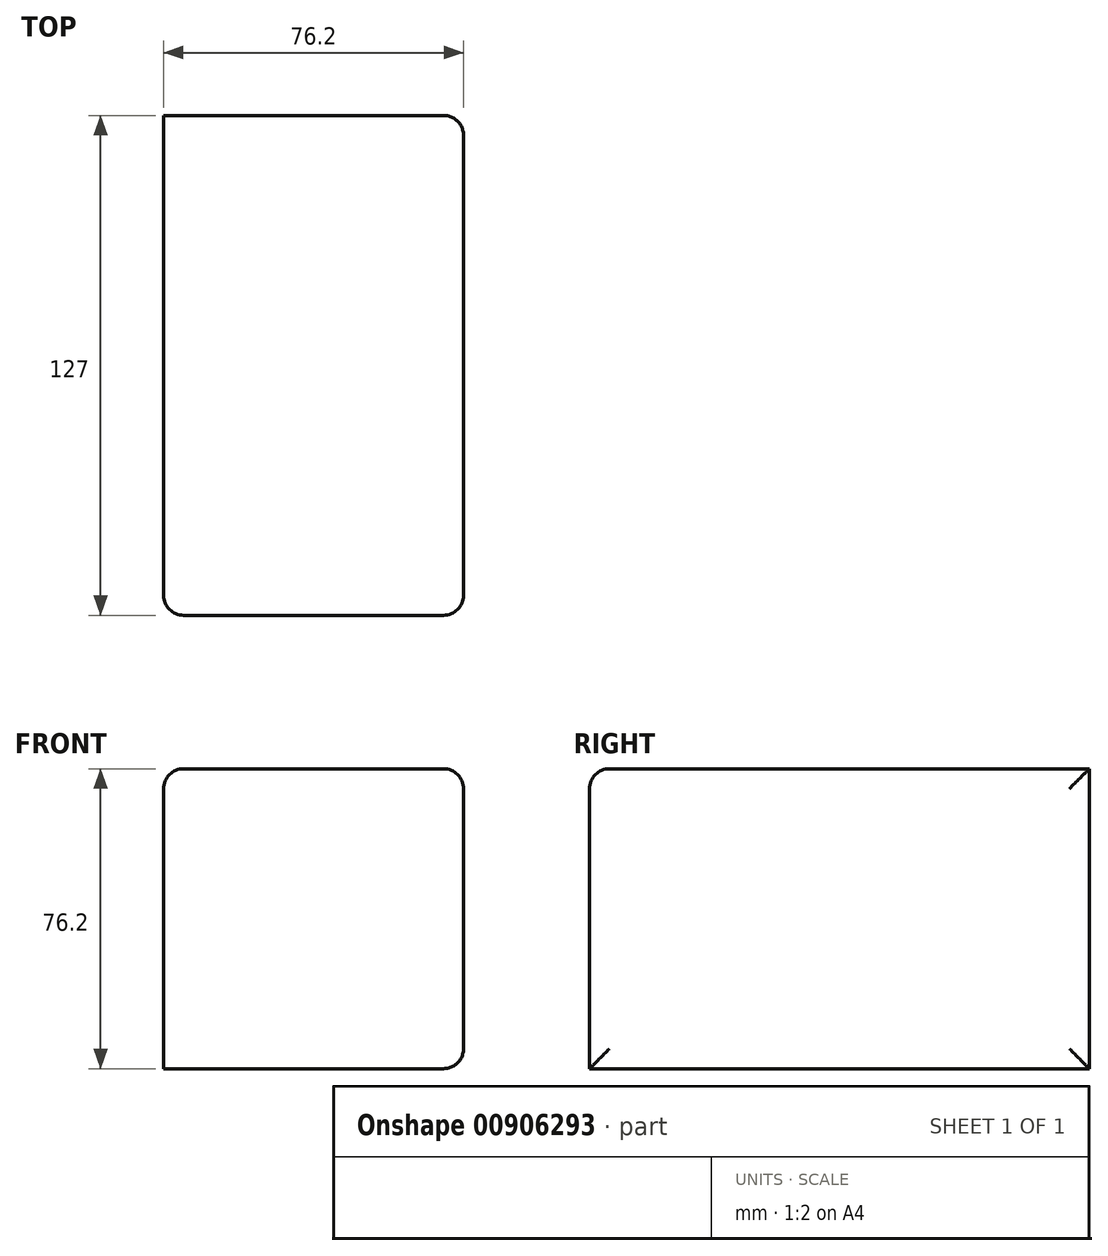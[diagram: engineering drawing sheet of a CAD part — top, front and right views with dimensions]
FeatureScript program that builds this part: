
annotation { "Feature Type Name" : "Feature", "Feature Type Description" : "" }
export const myFeature = defineFeature(function(context is Context, id is Id, definition is map)
    precondition{}
    {
        {
            var Q0;
            Q0=qCreatedBy(makeId("Front.planeOp"),FACE);
            var sketch = newSketch(context, id + "F0", { "sketchPlane" : qUnion([Q0])});
            skLineSegment(sketch, "E0", {"start": v(-38.1, 38.1) * mm, "end": v(-38.1, -38.1) * mm});
            skLineSegment(sketch, "E1", {"start": v(-38.1, -38.1) * mm, "end": v(38.1, -38.1) * mm});
            skLineSegment(sketch, "E2", {"start": v(38.1, -38.1) * mm, "end": v(38.1, 38.1) * mm});
            skLineSegment(sketch, "E3", {"start": v(38.1, 38.1) * mm, "end": v(-38.1, 38.1) * mm});
            skLineSegment(sketch, "E4", {"start": v(-38.1, 38.1) * mm, "end": v(38.1, -38.1) * mm, "construction": true});
            skSolve(sketch);
        }
        {
            var Q0;
            Q0=makeQuery(id+"F0.imprint","IMPRINT",FACE,{"disambiguationData":[TD([[makeQuery(id+"F0.imprint","IMPRINT",EDGE,{"derivedFrom":sQuery(id+"F0.wireOp",EDGE,"E0")}),1.0]])]});
            extrude(context, id + "F1", {"entities" : qUnion([Q0]), "endBound" : BoundingType.SYMMETRIC, "depth" : 127 * mm, "offsetDistance" : 25.4 * mm});
        }
        {
            var Q0;
            Q0=makeQuery(id+"F1.opExtrude","SWEPT_EDGE",EDGE,{"disambiguationData":[OSD([sQuery(id+"F0.wireOp",EDGE,"E0"),sQuery(id+"F0.wireOp",EDGE,"E3")])]});
            var Q1;
            Q1=makeQuery(id+"F1.opExtrude","CAP_EDGE",EDGE,{"disambiguationData":[OSD([sQuery(id+"F0.wireOp",EDGE,"E3")])],"isStart":false});
            var Q2;
            Q2=makeQuery(id+"F1.opExtrude","SWEPT_EDGE",EDGE,{"disambiguationData":[OSD([sQuery(id+"F0.wireOp",EDGE,"E2"),sQuery(id+"F0.wireOp",EDGE,"E3")])]});
            var Q3;
            Q3=makeQuery(id+"F1.opExtrude","CAP_EDGE",EDGE,{"disambiguationData":[OSD([sQuery(id+"F0.wireOp",EDGE,"E2")])],"isStart":false});
            var Q4;
            Q4=makeQuery(id+"F1.opExtrude","CAP_EDGE",EDGE,{"disambiguationData":[OSD([sQuery(id+"F0.wireOp",EDGE,"E0")])],"isStart":false});
            var Q5;
            Q5=makeQuery(id+"F1.opExtrude","SWEPT_FACE",FACE,{"disambiguationData":[OSD([sQuery(id+"F0.wireOp",EDGE,"E2")])]});
            fillet(context, id + "F2", {"entities" : qUnion([Q0, Q1, Q2, Q3, Q4, Q5]), "radius" : 5.08 * mm, "tangentPropagation" : true, "allowEdgeOverflow" : false});
        }
    });
